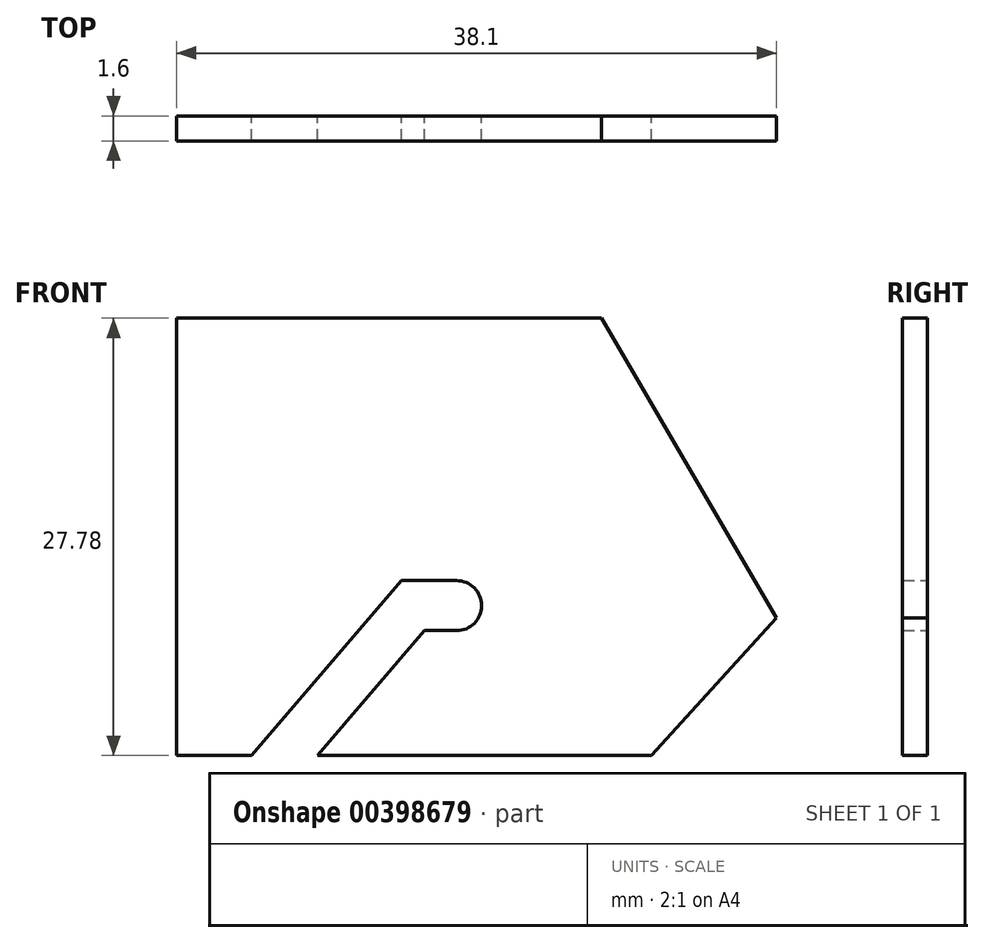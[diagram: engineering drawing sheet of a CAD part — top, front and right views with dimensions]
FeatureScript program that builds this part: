
annotation { "Feature Type Name" : "Feature", "Feature Type Description" : "" }
export const myFeature = defineFeature(function(context is Context, id is Id, definition is map)
    precondition{}
    {
        {
            var Q0;
            Q0=qCreatedBy(makeId("Front.planeOp"),FACE);
            var sketch = newSketch(context, id + "F0", { "sketchPlane" : qUnion([Q0])});
            skLineSegment(sketch, "E0.bottom", {"start": v(-19.05, 14.29) * mm, "end": v(7.94, 14.29) * mm});
            skLineSegment(sketch, "E0.top", {"start": v(-19.05, -13.5) * mm, "end": v(-14.29, -13.5) * mm});
            skLineSegment(sketch, "E0.left", {"start": v(-19.05, 14.29) * mm, "end": v(-19.05, -13.5) * mm});
            skPoint(sketch, "E0.middle", {"position": v(0, 0) * mm});
            skLineSegment(sketch, "E1", {"start": v(11.11, -13.5) * mm, "end": v(19.05, -4.76) * mm});
            skLineSegment(sketch, "E2", {"start": v(7.94, 14.29) * mm, "end": v(19.05, -4.76) * mm});
            skLineSegment(sketch, "E3", {"start": v(-14.29, -13.5) * mm, "end": v(-4.76, -2.38) * mm});
            skLineSegment(sketch, "E4", {"start": v(-4.76, -2.38) * mm, "end": v(-1.26, -2.38) * mm});
            skLineSegment(sketch, "E5", {"start": v(-10.1, -13.5) * mm, "end": v(-3.3, -5.56) * mm});
            skLineSegment(sketch, "E6", {"start": v(-3.3, -5.56) * mm, "end": v(-1.26, -5.56) * mm});
            skArc(sketch, "E7", {"start": v(-1.26, -5.56) * mm, "mid": v(0.32, -3.97) * mm, "end": v(-1.26, -2.38) * mm});
            skLineSegment(sketch, "E8.trimOffspring", {"start": v(-10.1, -13.5) * mm, "end": v(11.11, -13.5) * mm});
            skSolve(sketch);
        }
        {
            var Q0;
            Q0 = qSketchRegion(id + "F0", true);
            extrude(context, id + "F1", {"entities" : qUnion([Q0]), "endBound" : BoundingType.SYMMETRIC, "depth" : 1.6 * mm});
        }
    });
